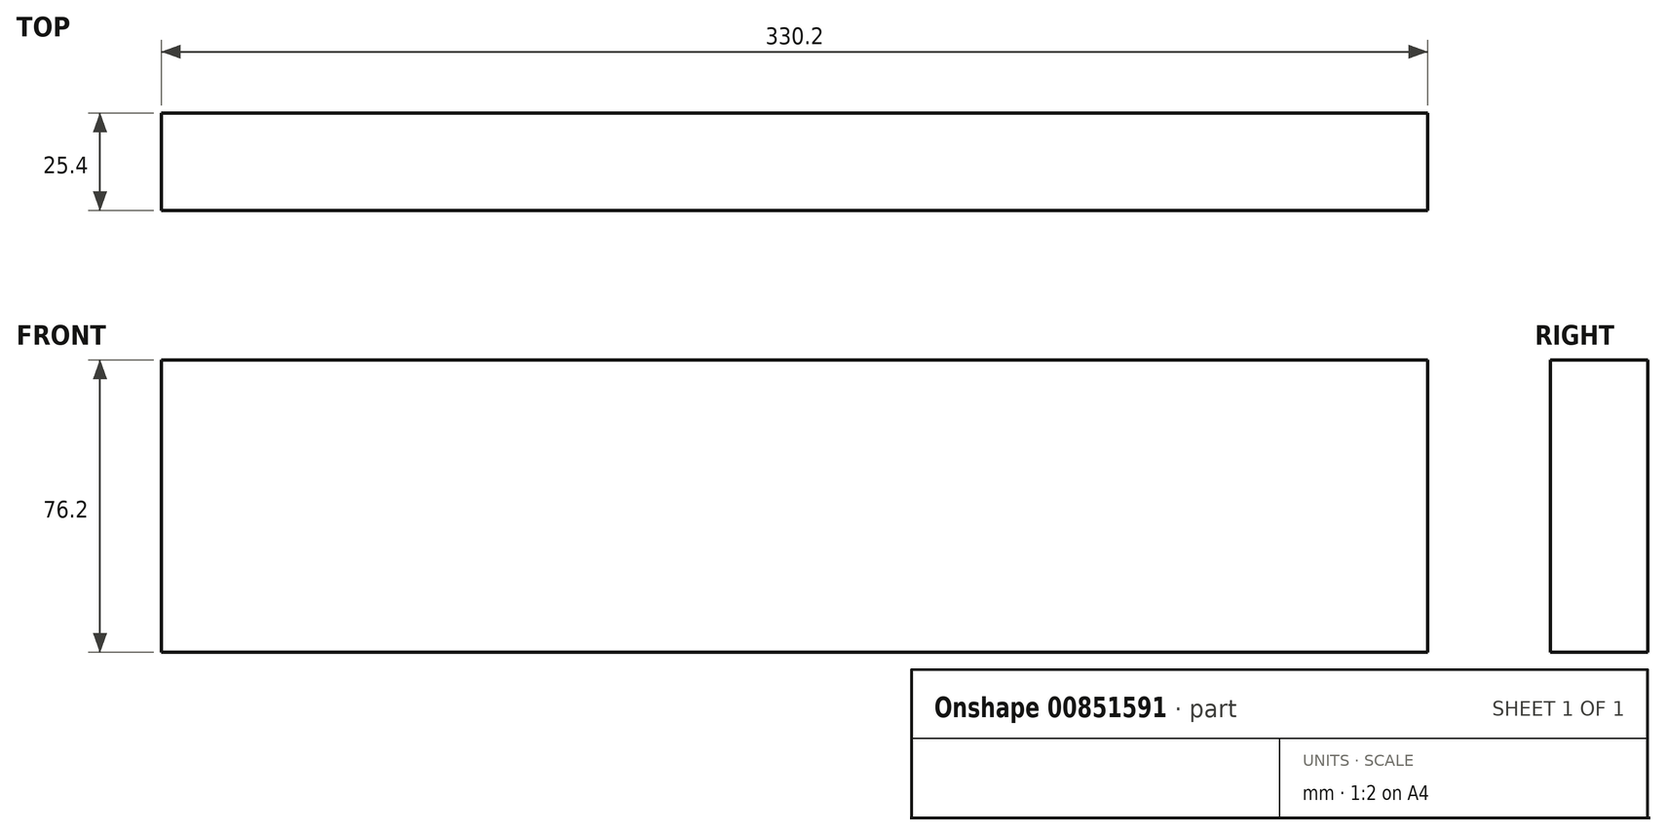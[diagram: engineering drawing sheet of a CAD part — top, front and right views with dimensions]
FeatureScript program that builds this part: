
annotation { "Feature Type Name" : "Feature", "Feature Type Description" : "" }
export const myFeature = defineFeature(function(context is Context, id is Id, definition is map)
    precondition{}
    {
        {
            var Q0;
            Q0=qCreatedBy(makeId("Front.planeOp"),FACE);
            var sketch = newSketch(context, id + "F0", { "sketchPlane" : qUnion([Q0])});
            skLineSegment(sketch, "E0.bottom", {"start": v(-172.01, 73.68) * mm, "end": v(158.19, 73.68) * mm});
            skLineSegment(sketch, "E0.top", {"start": v(-172.01, -2.52) * mm, "end": v(158.19, -2.52) * mm});
            skLineSegment(sketch, "E0.left", {"start": v(-172.01, 73.68) * mm, "end": v(-172.01, -2.52) * mm});
            skLineSegment(sketch, "E0.right", {"start": v(158.19, 73.68) * mm, "end": v(158.19, -2.52) * mm});
            skSolve(sketch);
        }
        {
            var Q0;
            Q0 = qSketchRegion(id + "F0", true);
            extrude(context, id + "F1", {"entities" : qUnion([Q0]), "depth" : 25.4 * mm, "offsetDistance" : 25.4 * mm});
        }
    });
